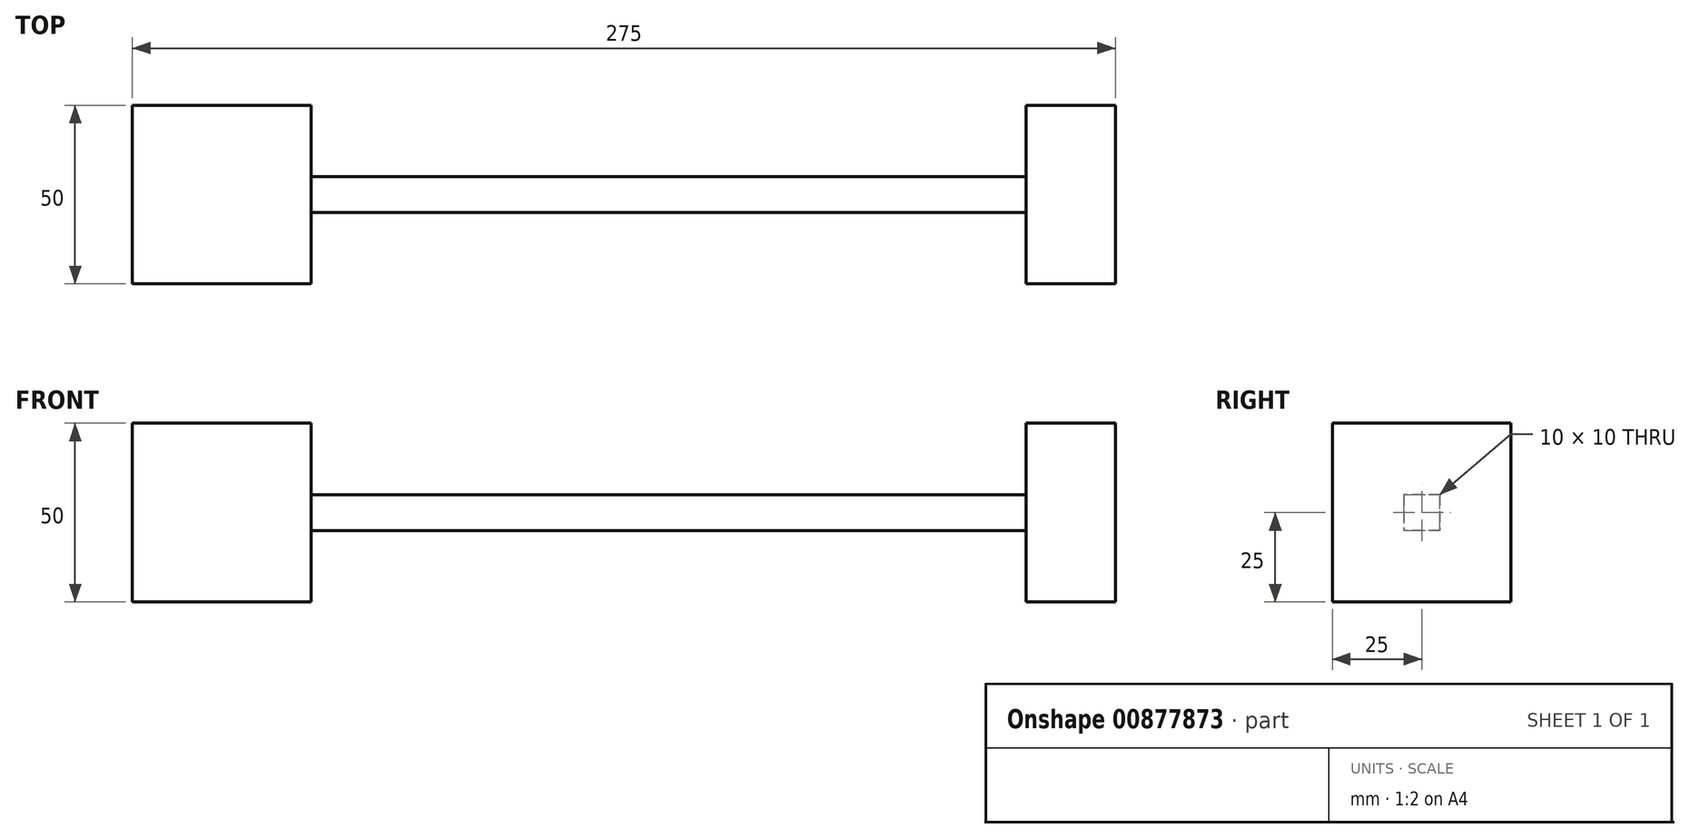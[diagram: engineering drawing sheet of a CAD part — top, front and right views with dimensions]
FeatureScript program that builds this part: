
annotation { "Feature Type Name" : "Feature", "Feature Type Description" : "" }
export const myFeature = defineFeature(function(context is Context, id is Id, definition is map)
    precondition{}
    {
        {
            var Q0;
            Q0=qCreatedBy(makeId("Top.planeOp"),FACE);
            var sketch = newSketch(context, id + "F0", { "sketchPlane" : qUnion([Q0])});
            skLineSegment(sketch, "E0.bottom", {"start": v(0, 0) * mm, "end": v(50, 0) * mm});
            skLineSegment(sketch, "E0.top", {"start": v(0, 50) * mm, "end": v(50, 50) * mm});
            skLineSegment(sketch, "E0.left", {"start": v(0, 0) * mm, "end": v(0, 50) * mm});
            skLineSegment(sketch, "E0.right", {"start": v(50, 0) * mm, "end": v(50, 50) * mm});
            skSolve(sketch);
        }
        {
            var Q0;
            Q0=makeQuery(id+"F0.imprint","IMPRINT",FACE,{"disambiguationData":[TD([[makeQuery(id+"F0.imprint","IMPRINT",EDGE,{"derivedFrom":sQuery(id+"F0.wireOp",EDGE,"E0.bottom")}),1.0]])]});
            extrude(context, id + "F1", {"entities" : qUnion([Q0]), "depth" : 50 * mm, "offsetDistance" : 25 * mm});
        }
        {
            var Q0;
            Q0=makeQuery(id+"F1.opExtrude","SWEPT_FACE",FACE,{"disambiguationData":[OSD([sQuery(id+"F0.wireOp",EDGE,"E0.right")])]});
            var sketch = newSketch(context, id + "F2", { "sketchPlane" : qUnion([Q0])});
            skLineSegment(sketch, "E1.bottom", {"start": v(30, 30) * mm, "end": v(20, 30) * mm});
            skLineSegment(sketch, "E1.top", {"start": v(30, 20) * mm, "end": v(20, 20) * mm});
            skLineSegment(sketch, "E1.left", {"start": v(30, 30) * mm, "end": v(30, 20) * mm});
            skLineSegment(sketch, "E1.right", {"start": v(20, 30) * mm, "end": v(20, 20) * mm});
            skPoint(sketch, "E1.middle", {"position": v(25, 25) * mm});
            skPoint(sketch, "E1.middle.positionSnap0", {"position": v(0, 25) * mm});
            skPoint(sketch, "E1.middle.positionSnap1", {"position": v(25, 50) * mm});
            skPoint(sketch, "E1.centerSnap0", {"position": v(0, 25) * mm});
            skPoint(sketch, "E1.centerSnap1", {"position": v(25, 50) * mm});
            skSolve(sketch);
        }
        {
            var Q0;
            Q0=makeQuery(id+"F2.imprint","IMPRINT",FACE,{"disambiguationData":[TD([[makeQuery(id+"F2.imprint","IMPRINT",EDGE,{"derivedFrom":sQuery(id+"F2.wireOp",EDGE,"E1.bottom")}),1.0]])]});
            var Q1;
            Q1 = qSketchRegion(id + "F4", true);
            extrude(context, id + "F3", {"entities" : qUnion([Q0, Q1]), "operationType" : NewBodyOperationType.ADD, "depth" : 200 * mm, "offsetDistance" : 25 * mm});
        }
        {
            var Q0;
            Q0=makeQuery(id+"F3.opExtrude","CAP_FACE",FACE,{"disambiguationData":[OSD([sQuery(id+"F2.wireOp",EDGE,"E1.bottom"),sQuery(id+"F2.wireOp",EDGE,"E1.top"),sQuery(id+"F2.wireOp",EDGE,"E1.left"),sQuery(id+"F2.wireOp",EDGE,"E1.right")])],"isStart":false});
            var sketch = newSketch(context, id + "F4", { "sketchPlane" : qUnion([Q0])});
            skLineSegment(sketch, "E2.bottom", {"start": v(50, 50) * mm, "end": v(0, 50) * mm});
            skLineSegment(sketch, "E2.top", {"start": v(50, 0) * mm, "end": v(0, 0) * mm});
            skLineSegment(sketch, "E2.left", {"start": v(50, 50) * mm, "end": v(50, 0) * mm});
            skLineSegment(sketch, "E2.right", {"start": v(0, 50) * mm, "end": v(0, 0) * mm});
            skPoint(sketch, "E2.middle", {"position": v(25, 25) * mm});
            skPoint(sketch, "E2.middle.positionSnap0", {"position": v(25, 30) * mm});
            skPoint(sketch, "E2.middle.positionSnap1", {"position": v(30, 25) * mm});
            skPoint(sketch, "E2.centerSnap0", {"position": v(25, 30) * mm});
            skPoint(sketch, "E2.centerSnap1", {"position": v(30, 25) * mm});
            skSolve(sketch);
        }
        {
            var Q0;
            Q0 = qSketchRegion(id + "F4", true);
            extrude(context, id + "F5", {"entities" : qUnion([Q0]), "operationType" : NewBodyOperationType.ADD, "depth" : 25 * mm, "offsetDistance" : 25 * mm});
        }
    });
